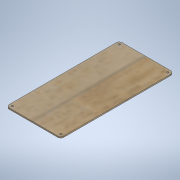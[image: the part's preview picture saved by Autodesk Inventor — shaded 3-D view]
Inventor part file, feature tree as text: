
AUTODESK INVENTOR PART (.ipt)
format: ipt  version: 2020.3 (Build 243373000, 373)  size: 148,480 bytes
history: native  units: mm
features: sketch x3, hole x2, other x1, extrude x1, fillet x1
ambient origin geometry x8: Origin, YZ Plane, XZ Plane, XY Plane, X Axis, Y Axis, Z Axis, Center Point
bodies: Body1 (feature_tree)
feature tree (8):
  other  "ソリッド1"
  extrude  "押し出し1"  Depth=169.0mm
  fillet  "フィレット1"  Radius=2.0mm
  hole  "穴2"  [1 undecoded]
  hole  "穴3"  [1 undecoded]
  sketch  "スケッチ1"
  sketch  "スケッチ3"
  sketch  "スケッチ4"
note: 2 required parameter values undecoded (feature->parameter linkage not recoverable at this tier; creation-order binding heuristic only, values carry confidence <= 0.55)
